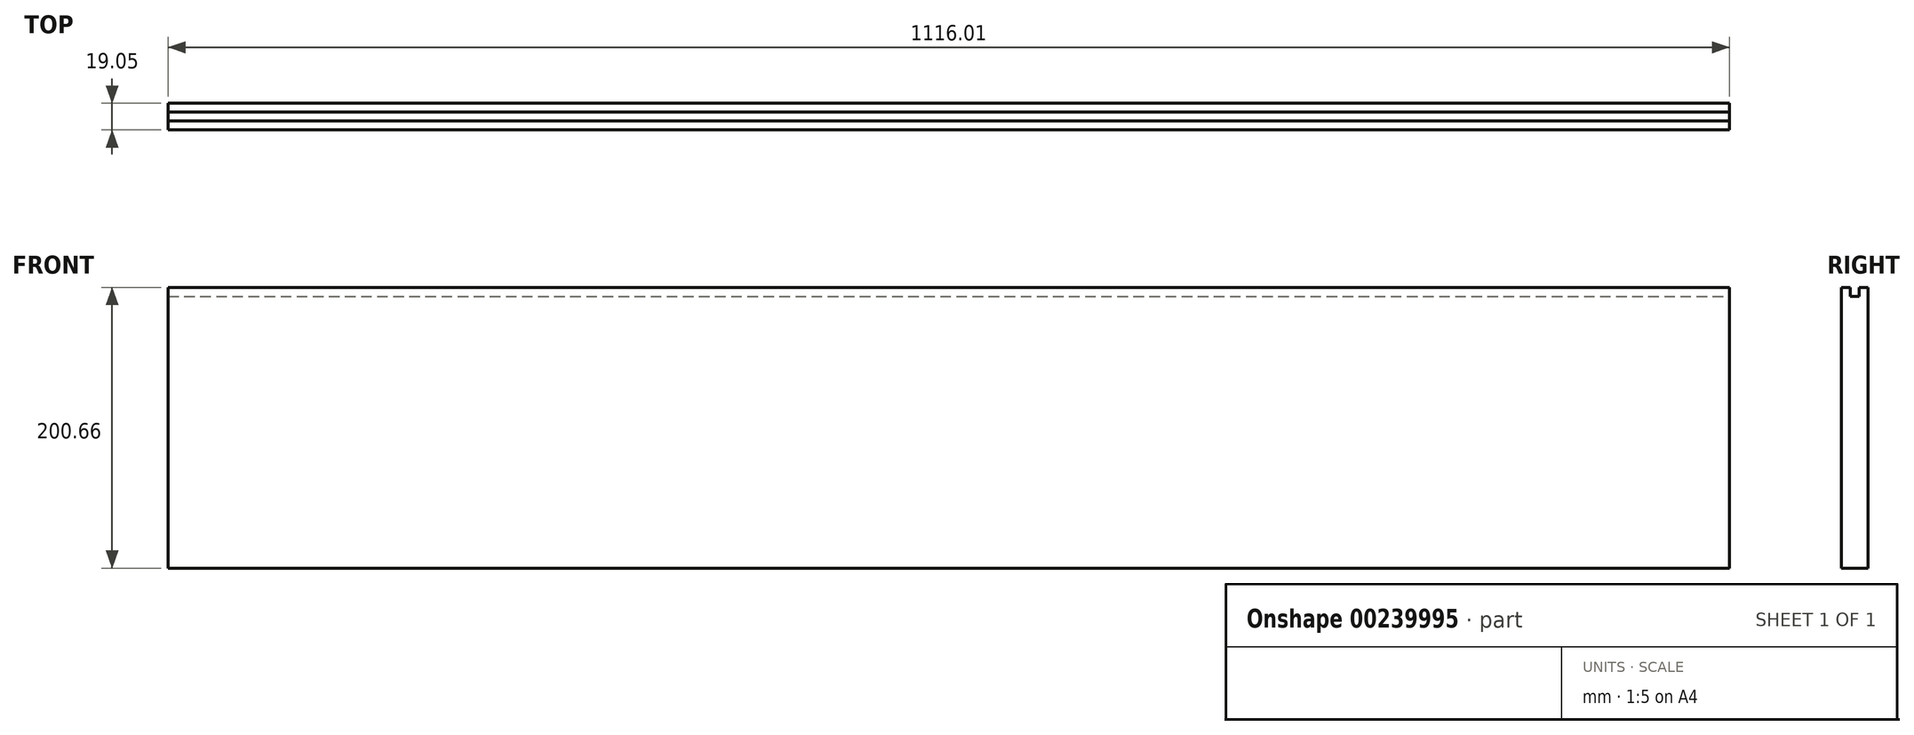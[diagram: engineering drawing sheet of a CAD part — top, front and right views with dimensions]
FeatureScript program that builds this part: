
annotation { "Feature Type Name" : "Feature", "Feature Type Description" : "" }
export const myFeature = defineFeature(function(context is Context, id is Id, definition is map)
    precondition{}
    {
        {
            var Q0;
            Q0=qCreatedBy(makeId("Front.planeOp"),FACE);
            var sketch = newSketch(context, id + "F0", { "sketchPlane" : qUnion([Q0])});
            skLineSegment(sketch, "E0.bottom", {"start": v(-599.98, -302.13) * mm, "end": v(516.03, -302.13) * mm});
            skLineSegment(sketch, "E0.top", {"start": v(-599.98, -502.8) * mm, "end": v(516.03, -502.8) * mm});
            skLineSegment(sketch, "E0.left", {"start": v(-599.98, -302.13) * mm, "end": v(-599.98, -502.8) * mm});
            skLineSegment(sketch, "E0.right", {"start": v(516.03, -302.13) * mm, "end": v(516.03, -502.8) * mm});
            skSolve(sketch);
        }
        {
            var Q0;
            Q0=makeQuery(id+"F0.imprint","IMPRINT",FACE,{"disambiguationData":[TD([[makeQuery(id+"F0.imprint","IMPRINT",EDGE,{"derivedFrom":sQuery(id+"F0.wireOp",EDGE,"E0.bottom")}),-1.0]])]});
            extrude(context, id + "F1", {"entities" : qUnion([Q0]), "depth" : 19.05 * mm, "offsetDistance" : 25.4 * mm});
        }
        {
            var Q0;
            Q0=makeQuery(id+"F1.opExtrude","SWEPT_FACE",FACE,{"disambiguationData":[OSD([sQuery(id+"F0.wireOp",EDGE,"E0.right")])]});
            var sketch = newSketch(context, id + "F2", { "sketchPlane" : qUnion([Q0])});
            skLineSegment(sketch, "E1.bottom", {"start": v(-12.7, -302.13) * mm, "end": v(-6.35, -302.13) * mm});
            skLineSegment(sketch, "E1.top", {"start": v(-12.7, -308.48) * mm, "end": v(-6.35, -308.48) * mm});
            skLineSegment(sketch, "E1.left", {"start": v(-12.7, -302.13) * mm, "end": v(-12.7, -308.48) * mm});
            skLineSegment(sketch, "E1.right", {"start": v(-6.35, -302.13) * mm, "end": v(-6.35, -308.48) * mm});
            skSolve(sketch);
        }
        {
            var Q0;
            Q0=qSketchRegion(id+"F2",true);
            extrude(context, id + "F3", {"entities" : qUnion([Q0]), "operationType" : NewBodyOperationType.REMOVE, "endBound" : BoundingType.THROUGH_ALL, "oppositeDirection" : true, "depth" : 25.4 * mm, "offsetDistance" : 25.4 * mm});
        }
    });
